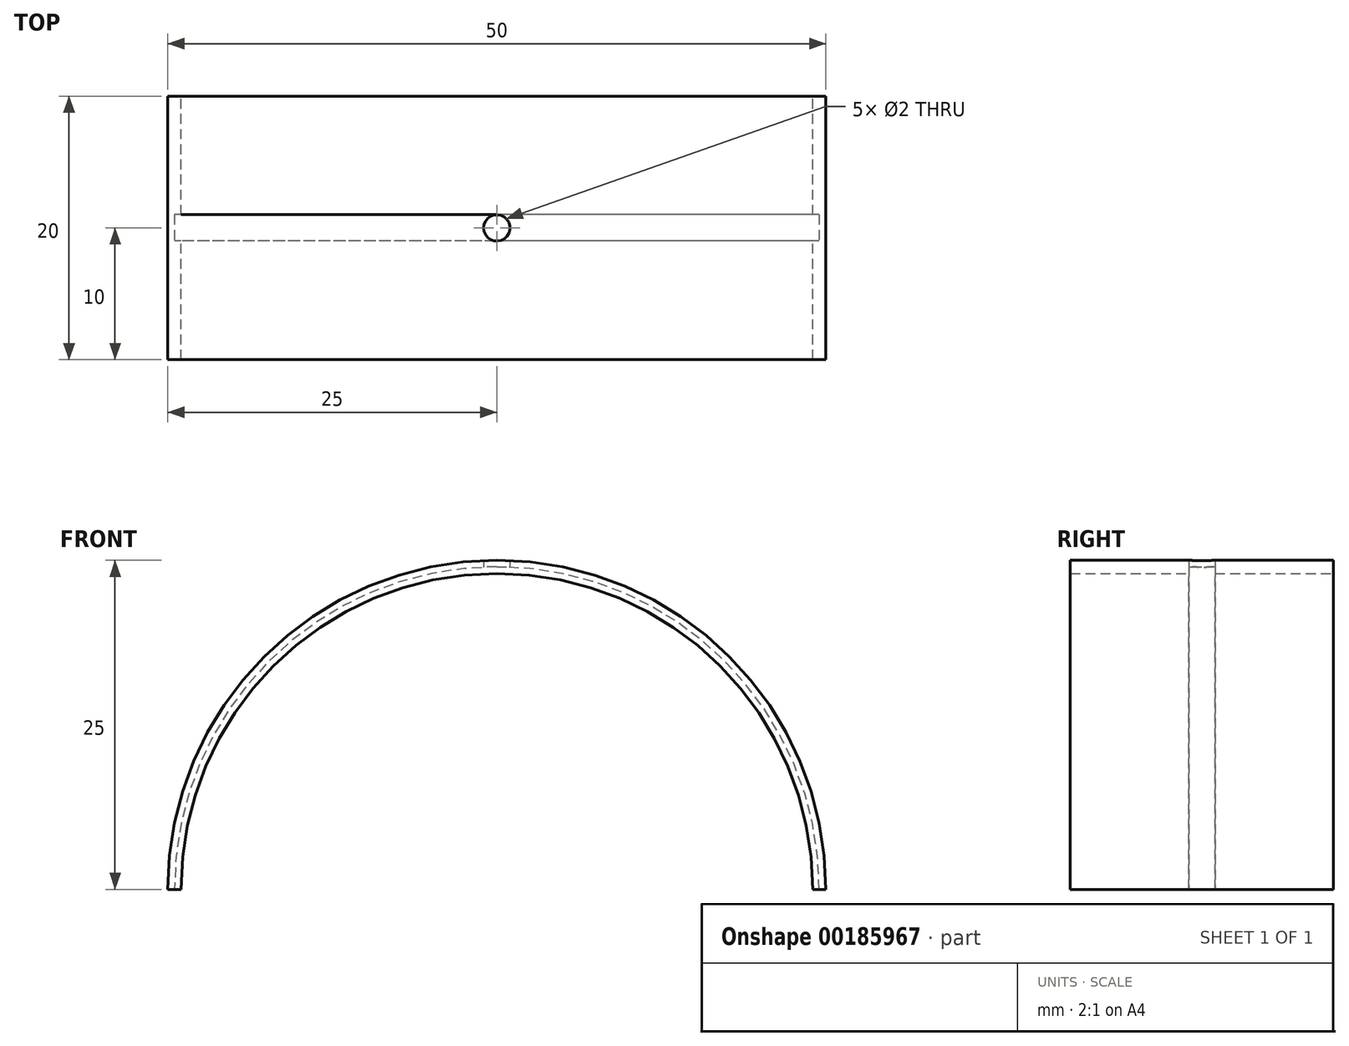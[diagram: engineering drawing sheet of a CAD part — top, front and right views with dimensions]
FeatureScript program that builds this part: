
annotation { "Feature Type Name" : "Feature", "Feature Type Description" : "" }
export const myFeature = defineFeature(function(context is Context, id is Id, definition is map)
    precondition{}
    {
        {
            var Q0;
            Q0=qCreatedBy(makeId("Front.planeOp"),FACE);
            var sketch = newSketch(context, id + "F0", { "sketchPlane" : qUnion([Q0])});
            skArc(sketch, "E0", {"start": v(25, 0) * mm, "mid": v(0, 25) * mm, "end": v(-25, 0) * mm});
            skArc(sketch, "E1.0", {"start": v(24, 0) * mm, "mid": v(0, 24) * mm, "end": v(-24, 0) * mm});
            skLineSegment(sketch, "E2", {"start": v(-25, 0) * mm, "end": v(-24, 0) * mm});
            skPoint(sketch, "E3.orphan", {"position": v(-27.21, 0) * mm});
            skLineSegment(sketch, "E4.trimOffspring", {"start": v(24, 0) * mm, "end": v(25, 0) * mm});
            skSolve(sketch);
        }
        {
            var Q0;
            Q0 = qSketchRegion(id + "F0", true);
            extrude(context, id + "F1", {"entities" : qUnion([Q0]), "depth" : 20 * mm, "symmetric" : true});
        }
        {
            var Q0;
            Q0=qCreatedBy(makeId("Top.planeOp"),FACE);
            var sketch = newSketch(context, id + "F2", { "sketchPlane" : qUnion([Q0])});
            skLineSegment(sketch, "E5.bottom", {"start": v(-24.5, 1) * mm, "end": v(-24, 1) * mm});
            skLineSegment(sketch, "E5.top", {"start": v(-24.5, -1) * mm, "end": v(-24, -1) * mm});
            skLineSegment(sketch, "E5.left", {"start": v(-24.5, 1) * mm, "end": v(-24.5, -1) * mm});
            skLineSegment(sketch, "E5.right", {"start": v(-24, 1) * mm, "end": v(-24, -1) * mm});
            skPoint(sketch, "E5.middle", {"position": v(-24.25, 0) * mm});
            skSolve(sketch);
        }
        {
            var Q0;
            Q0 = qSketchRegion(id + "F2", true);
            var Q1;
            Q1=makeQuery(id+"F1.opExtrude","SWEPT_FACE",FACE,{"disambiguationData":[OSD([sQuery(id+"F0.wireOp",EDGE,"E1.0")])]});
            revolve(context, id + "F3", {"operationType" : NewBodyOperationType.REMOVE, "entities" : qUnion([Q0]), "axis" : qUnion([Q1]), "revolveType" : RevolveType.FULL, "oppositeDirection" : true});
        }
        {
            var Q0;
            Q0=qCreatedBy(makeId("Top.planeOp"),FACE);
            var sketch = newSketch(context, id + "F4", { "sketchPlane" : qUnion([Q0])});
            skCircle(sketch, "E6", {"center": v(0, 0) * mm, "radius": 1 * mm});
            skSolve(sketch);
        }
        {
            var Q0;
            Q0 = qSketchRegion(id + "F4", true);
            extrude(context, id + "F5", {"entities" : qUnion([Q0]), "operationType" : NewBodyOperationType.REMOVE, "endBound" : BoundingType.THROUGH_ALL, "depth" : 25 * mm});
        }
    });
